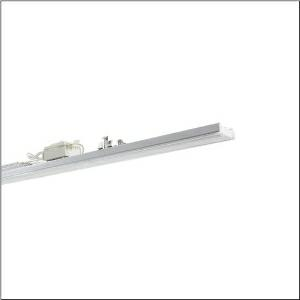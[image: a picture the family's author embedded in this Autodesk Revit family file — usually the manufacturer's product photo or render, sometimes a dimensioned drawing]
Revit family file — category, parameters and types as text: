
# Revit family: licross_r__11_recessed_ho_51tl12dv4m2m_69f1
name_source: partatom
category: Lighting Fixtures
units: mm (PartAtom-declared; Revit-internal decimal feet)

## family parameters
Cut with Voids When Loaded = No
Host = Face
Light Source = No
Part Type = Normal
Room Calculation Point = No
Round Connector Dimension = Use Diameter
Shared = No

## types (1)
- --- (1 x LED, 27150 lm, 150.5 W, 4000K)
    Apparent Load = 150 VA
    CIE Flux Codes = 66 91 98 100 100
    Color Rendering = 80
    Color Temperature = 4000K
    Default Elevation = 1800 mm
    Description = Licross® 11 Recessed HO, luminaire insert, of sheet steel, coil coated, white, length: 2.250mm, width: 66mm, height: 67mm, LED rated luminous flux: 27.150lm, light colour: 840, control gear: DALI 2, with plug, 5-pole, with phase selection, mains connection: 220..240V, AC, 50/60Hz, rated input power: 151W, halogen-free wiring, primary optical cover: cover, of PMMA, light emission: direct distribution, primary light characteristic: symmetric, protection rating (complete): IP40, insulation class (complete): insulation class I (protective earthing), certification: CE, ENEC, VDE, UKCA, protection symbol: D if used in an environment without relevant dust loads with corresponding accessories, impact resistance: IK06, permissible ambient temperature for indoor applications: -40..+35°C, corresponds to IFS (International Featured Standards) requirements for safety and quality in the food industry, reducing of maximum allowable ambient temperature of 5°C with ceiling mounting, LABS conformity tested according to VDMA 24364:2018-05, packaging unit: 1 piece
    Height = 58 mm
    Lamp = 1 x LED
    Lamp Light Flux = 27150 lm
    Lamp Power = 150.5 W
    Lamp count = 1
    Length = 2250 mm
    Luminous efficacy = 180 lm/W
    Manufacturer = Siteco
    ModVariant = No
    Model = 51TL12DV4M2M
    Mounting Place = Ceiling
    Mounting Type = Pendant
    Number of Poles = 1
    OnlyDefault = Yes
    Power Factor = 1
    Product Name = Licross® 11 Recessed HO
    Product group = luminaire insert
    ProductGroupID = 902
    Protection Class = Protection class I
    Protection Degree = IP 40
    RLX_Detail_Level = 1
    RLX_Emergency_Light_Flux = 0 lm
    RLX_Emergency_Type = 0
    RLX_Emergency_Type_DB = No
    RlxData = <blob elided: 29561 chars, md5=302b644a>
    Socket = socket
    Standby Power = 0 W
    System Light Flux = 27150 lm
    System Power = 150 W
    Type Comments = factory setting: luminous flux: 100 % | dim-lin: 254 | 690 mA
    Type Image = l_1296930.jpg
    URL = http://relux.com
    VarID = @adj_099692
    Voltage = 0 V
    Weight = 0.00 kg
    Width = 66 mm

## geometry (parser evidence)
native form markers: Blend x4, Sweep x9
no freeform markers — native parametric forms only
